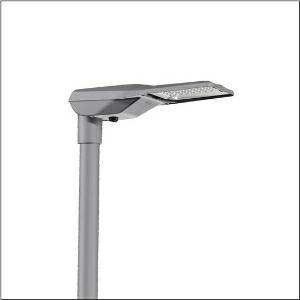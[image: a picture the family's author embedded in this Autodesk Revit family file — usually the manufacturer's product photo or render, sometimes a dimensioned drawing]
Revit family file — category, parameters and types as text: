
# Revit family: streetlight_sl_21_mini___p0_5a_5xe2v33r08gb_5767
name_source: partatom
category: Lighting Fixtures
units: mm (PartAtom-declared; Revit-internal decimal feet)

## family parameters
Cut with Voids When Loaded = No
Host = Face
Light Source = No
Part Type = Normal
Room Calculation Point = No
Round Connector Dimension = Use Diameter
Shared = No

## types (1)
- --- (1 x LED, 5840 lm, 40.4 W, 3000K)
    Apparent Load = 40 VA
    CIE Flux Codes = 37 73 96 100 100
    Color Rendering = 70
    Color Temperature = 3000K
    Default Elevation = 1800 mm
    Description = Streetlight SL 21 mini, mast luminaire, primary light control with lens, of PMMA, primary optical cover: cover, of toughened safety glass, transparent, light distribution: P0.5a, light emission: direct distribution, primary light characteristic: asymmetric, installation type: post-top, side-entry, LED, High Power LED, rated luminous flux: 5.840lm, luminous efficacy: 145lm/W, light colour: 730, colour temperature: 3000K, control gear: D4i, control: pre-setting: logarithmic dimming characteristic, flexible luminous flux parameterisation, time-dependent luminous flux control, constant luminous flux control, overheat protection, mains connection: 220..240V, AC, 50/60Hz, start of lifetime: 40W, end of service life: 41W, reduction: 19W, luminaire housing, of diecast aluminium, powder-coated, SITECO metallic grey (DB 702S), corrosivity category C5 high according to DIN EN ISO 12944, multi-level sealing system, sealing non-destructively replaceable, inclination adjustable: 0°, 5°, 10°, 15°, please order mast flange separately, length: 628mm, width: 235mm, height: 110mm, mast flange for spigot size: 42mm (side-entry): 5XC10008XM4, 60/48mm (side-entry/post-top): 5XC10108XM2, 76/60mm (side-entry/post-top): 5XC10108XM1, mounting height: 4..8m, Smart Interface below, protection rating (complete): IP66, insulation class (complete): insulation class II (safety insulation), certification: CE, ENEC, ENEC+, VDE, impact resistance: IK10, permissible operating ambient temperature for outdoor applications: -40..+50°C, standard-compliant lighting for roads and squares, packaging unit: 1 piece

Light Distribution: P0.5a
    Height = 110 mm
    Lamp = 1 x LED
    Lamp Light Flux = 5840 lm
    Lamp Power = 40.4 W
    Lamp count = 1
    Length = 625 mm
    Luminous efficacy = 145 lm/W
    Manufacturer = Siteco
    ModVariant = No
    Model = 5XE2V33R08GB
    Number of Poles = 1
    OnlyDefault = Yes
    Power Factor = 1
    Product Name = Streetlight SL 21 mini | P0.5a
    Product group = mast luminaire | pylon top
    ProductGroupID = 6100
    Protection Class = Protection class II
    Protection Degree = IP 66
    RLX_Detail_Level = 1
    RLX_Emergency_Light_Flux = 0 lm
    RLX_Emergency_Type = 0
    RLX_Emergency_Type_DB = No
    RlxData = <blob elided: 91717 chars, md5=02b13880>
    Socket = socket
    Standby Power = 0 W
    System Light Flux = 5840 lm
    System Power = 40 W
    Type Comments = factory setting: luminous flux: 100 % | dim-lin: 254 | 812 mA
    Type Image = l_1003516.jpg
    URL = http://relux.com
    VarID = @adj_077319
    Voltage = 0 V
    Weight = 0.00 kg
    Width = 234 mm

## geometry (parser evidence)
native form markers: Blend x4, Sweep x10
no freeform markers — native parametric forms only
